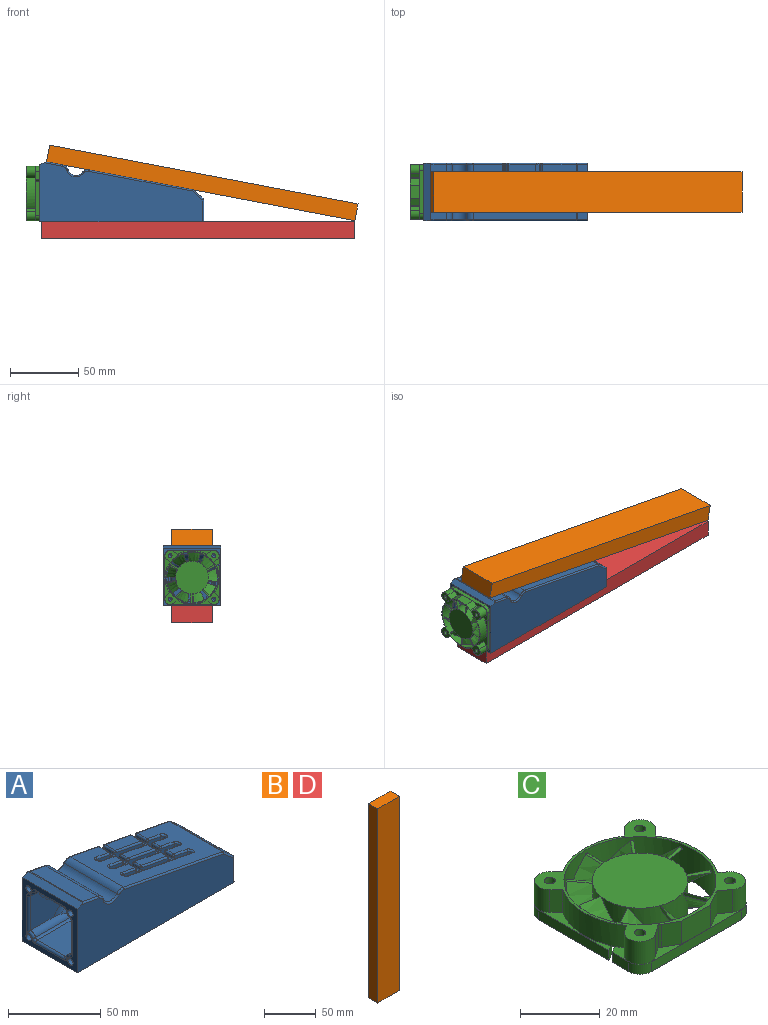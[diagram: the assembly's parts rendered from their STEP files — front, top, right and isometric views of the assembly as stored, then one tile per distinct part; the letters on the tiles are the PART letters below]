
ASSEMBLY  parts=4 mates=1
PART A: 266 faces, bbox 123.9x42.9x45.2 mm
  f0: plane 119.42x43.31mm, normal (0,-1,0), area 3799.1mm2, adj f2,f18,f19,f95,f96,f102,f110,f111
  f1: plane 119.42x43.31mm, normal (0,1,0), area 3711mm2, adj f2,f18,f19,f24,f26,f28,f75,f82
  f2: plane 42x42mm, normal (-1,0,0), area 549mm2, adj f0,f1,f18,f19,f43,f45,f47,f49
  f3: plane 28.92x13.78mm, normal (-1,0,0), area 281.8mm2, adj f10,f29,f78,f80,f81,f222,f223,f259
  f4: plane 75.7x40mm, normal (0.19,0,0.98), area 1748.4mm2, adj f103,f111,f118,f125,f131,f138,f139,f144
  f5: plane 19.65x5mm, normal (0.19,0,0.98), area 100mm2, adj f167,f168,f184,f185
  f6: plane 19.65x5mm, normal (0.19,0,0.98), area 100mm2, adj f107,f115,f121,f122
  f7: plane 19.65x7.5mm, normal (0.19,0,0.98), area 150mm2, adj f82,f84,f86,f87
  f8: plane 49.86x13.29mm, normal (0,1,0), area 175.6mm2, adj f29,f50,f52,f69,f107,f120,f127,f132
  f9: plane 49.86x13.29mm, normal (0,1,0), area 173.4mm2, adj f29,f53,f55,f155,f159,f164,f168,f174
  f10: plane 113.99x26.84mm, normal (0,0,1), area 2764.6mm2, adj f3,f15,f32,f33,f34,f35,f223,f246
  f11: cone r=2.58mm half-angle=59deg, axis (0,1,0), area 59.4mm2, adj f12,f40,f246,f249
  f12: torus R=11.59mm, axis (0,-1,0), area 95.8mm2, adj f11,f15,f40,f246
  f13: plane 21.06x5.74mm, normal (-0.19,0,-0.98), area 122.8mm2, adj f14,f36,f229,f232
  f14: plane 21.11x3.44mm, normal (0.37,0,-0.93), area 78mm2, adj f13,f229,f230,f232,f236,f237
  f15: plane 111.92x26.52mm, normal (0,-1,0), area 1378.2mm2, adj f10,f12,f16,f34,f35,f40,f223,f225
  f16: torus R=21mm, axis (0,-1,0), area 471.5mm2, adj f15,f30,f36,f227,f231,f234
  f17: plane 40x11.7mm, normal (0.19,0,0.98), area 476.4mm2, adj f90,f91,f96,f264
  f18: plane 42.19x4.92mm, normal (-0.37,0,0.93), area 213.5mm2, adj f0,f1,f2,f90,f91,f96
  f19: plane 119.42x42mm, normal (0,0,-1), area 5015.7mm2, adj f0,f1,f2,f100
  f20: plane 40x15.04mm, normal (1,0,0), area 601.6mm2, adj f95,f100,f108,f109
  f21: plane 40x7.68mm, normal (0.65,0,0.76), area 219.4mm2, adj f109,f110,f124,f125,f218,f219,f220,f221
  f22: cylinder r=6mm len=40mm, axis (0,1,0), area 527.5mm2, adj f97,f102,f261,f264
  f23: cone r=0mm half-angle=59deg, axis (0,1,0), area 24.8mm2, adj f24
  f24: cylinder r=2.6mm len=5.2mm, axis (0,1,0), area 49mm2, adj f1,f23
  f25: cone r=0mm half-angle=59deg, axis (0,1,0), area 24.8mm2, adj f26
  f26: cylinder r=2.6mm len=5.2mm, axis (0,1,0), area 49mm2, adj f1,f25
  f27: cone r=0mm half-angle=59deg, axis (0,1,0), area 24.8mm2, adj f28
  f28: cylinder r=2.6mm len=5.2mm, axis (0,1,0), area 49mm2, adj f1,f27
  f29: plane 79.71x28.72mm, normal (-0.19,0,-0.98), area 1654.8mm2, adj f3,f8,f9,f50,f51,f52,f53,f54
  f30: cylinder r=11mm len=17.03mm, axis (0,1,0), area 234.6mm2, adj f16,f36,f37,f228
  f31: plane 111.92x21.42mm, normal (0,1,0), area 1445.6mm2, adj f37,f222,f224,f243,f250,f255
  f32: cone r=2.58mm half-angle=59deg, axis (0,1,0), area 90.4mm2, adj f10,f35
  f33: cone r=2.58mm half-angle=59deg, axis (0,1,0), area 90.4mm2, adj f10,f34
  f34: torus R=11.59mm, axis (0,-1,0), area 115.8mm2, adj f10,f15,f33
  f35: torus R=11.59mm, axis (0,-1,0), area 115.8mm2, adj f10,f15,f32
  f36: cylinder r=10mm len=21.64mm, axis (0,1,0), area 148.6mm2, adj f13,f16,f30,f37,f231,f235
  f37: torus R=21mm, axis (0,-1,0), area 471.5mm2, adj f30,f31,f36,f226,f235,f240
  f38: cylinder r=4mm len=12.05mm, axis (-1,0,0), area 55.1mm2, adj f229,f230,f231,f234,f238,f239
  f39: cylinder r=4mm len=12.05mm, axis (-1,0,0), area 55.1mm2, adj f232,f235,f236,f240,f243,f244
  f40: cylinder r=4mm len=26.78mm, axis (-1,0,0), area 120.5mm2, adj f11,f12,f15,f248,f249
  f41: cylinder r=4mm len=112.42mm, axis (-1,0,0), area 441.4mm2, adj f253,f255,f257,f258,f259
  f42: cone r=0mm half-angle=59deg, axis (-1,0,0), area 14.7mm2, adj f43
  f43: cylinder r=2mm len=12mm, axis (-1,0,0), area 150.8mm2, adj f2,f42
  f44: cone r=0mm half-angle=59deg, axis (-1,0,0), area 14.7mm2, adj f45
  f45: cylinder r=2mm len=12mm, axis (-1,0,0), area 150.8mm2, adj f2,f44
  f46: cone r=0mm half-angle=59deg, axis (-1,0,0), area 14.7mm2, adj f47
  f47: cylinder r=2mm len=12mm, axis (-1,0,0), area 150.8mm2, adj f2,f46
  f48: cone r=0mm half-angle=59deg, axis (-1,0,0), area 14.7mm2, adj f49
  f49: cylinder r=2mm len=12mm, axis (-1,0,0), area 150.8mm2, adj f2,f48
  f50: cylinder r=1.5mm len=4.21mm, axis (0.19,0,0.98), area 18.8mm2, adj f8,f29,f51,f162
  f51: plane 49.86x13.29mm, normal (0,-1,0), area 175.6mm2, adj f29,f50,f52,f75,f87,f94,f99,f106
  f52: cylinder r=1.5mm len=4.21mm, axis (0.19,0,0.98), area 18.8mm2, adj f8,f29,f51,f139
  f53: cylinder r=1.5mm len=4.21mm, axis (0.19,0,0.98), area 18.8mm2, adj f9,f29,f54,f203
  f54: plane 49.86x13.29mm, normal (0,-1,0), area 175.6mm2, adj f29,f53,f55,f69,f122,f134,f141,f147
  f55: cylinder r=1.5mm len=4.21mm, axis (0.19,0,0.98), area 18.8mm2, adj f9,f29,f54,f173
  f56: cylinder r=1.5mm len=4.21mm, axis (0.19,0,0.98), area 18.8mm2, adj f29,f57,f59,f215
  f57: plane 49.86x13.29mm, normal (0,-1,0), area 173.4mm2, adj f29,f56,f58,f166,f175,f183,f184,f190
  f58: cylinder r=1.5mm len=4.21mm, axis (0.19,0,0.98), area 18.8mm2, adj f29,f57,f59,f209
  f59: plane 49.86x13.29mm, normal (0,1,0), area 200mm2, adj f29,f56,f58,f212
  f60: plane 5x0.98mm, normal (-0.98,0,0.19), area 5mm2, adj f155,f165,f166,f167
  f61: plane 5x0.98mm, normal (0.98,0,-0.19), area 5mm2, adj f181,f182,f194,f195
  f62: plane 5x0.98mm, normal (0.19,0,0.98), area 5mm2, adj f164,f165,f182,f183
  f63: plane 5x0.98mm, normal (0.98,0,-0.19), area 5mm2, adj f185,f186,f196,f197
  f64: plane 5x0.98mm, normal (-0.98,0,0.19), area 5mm2, adj f206,f207,f213,f214
  f65: plane 5x0.98mm, normal (0.19,0,0.98), area 5mm2, adj f197,f198,f205,f206
  f66: plane 5x0.98mm, normal (-0.98,0,0.19), area 5mm2, adj f120,f121,f133,f134
  f67: plane 5x0.98mm, normal (0.98,0,-0.19), area 5mm2, adj f145,f146,f153,f154
  f68: plane 5x0.98mm, normal (0.19,0,0.98), area 5mm2, adj f132,f133,f146,f147
  f69: plane 7x2.95mm, normal (0.98,0,-0.19), area 14.4mm2, adj f8,f54,f71,f115,f156,f169
  f70: plane 5x0.98mm, normal (-0.98,0,0.19), area 5mm2, adj f170,f171,f187,f188
  f71: plane 5x1.96mm, normal (0.19,0,0.98), area 10mm2, adj f69,f156,f169,f170
  f72: plane 7.5x0.98mm, normal (-0.98,0,0.19), area 7.5mm2, adj f85,f86,f93,f94
  f73: plane 7.5x0.98mm, normal (0.98,0,-0.19), area 7.5mm2, adj f104,f105,f118,f119
  f74: plane 7.5x0.98mm, normal (0.19,0,0.98), area 7.5mm2, adj f92,f93,f105,f106
  f75: plane 9.5x2.95mm, normal (0.98,0,-0.19), area 19.4mm2, adj f1,f51,f77,f84,f123,f135
  f76: plane 7.5x0.98mm, normal (-0.98,0,0.19), area 7.5mm2, adj f136,f137,f148,f149
  f77: plane 7.5x1.96mm, normal (0.19,0,0.98), area 15mm2, adj f75,f123,f135,f136
  f78: cylinder r=2.5mm len=5.92mm, axis (0.65,0,0.76), area 17.2mm2, adj f3,f29,f79,f80,f221
  f79: plane 21x2.34mm, normal (0.76,0,-0.65), area 64.8mm2, adj f29,f78,f81,f220
  f80: plane 21x2.48mm, normal (-0.76,0,0.65), area 68.7mm2, adj f3,f78,f81,f219
  f81: cylinder r=2.5mm len=5.92mm, axis (0.65,0,0.76), area 17.2mm2, adj f3,f29,f79,f80,f218
  f82: cylinder r=1mm len=20.82mm, axis (-0.98,0,0.19), area 32.2mm2, adj f1,f7,f83,f84
  f83: sphere r=1mm, area 1.6mm2, adj f82,f85,f86
  f84: cylinder r=1mm len=9.5mm, axis (0,-1,0), area 13.4mm2, adj f7,f75,f82,f87
  f85: cylinder r=1mm len=1.17mm, axis (0.19,0,0.98), area 1.6mm2, adj f1,f72,f83,f88
  f86: cylinder r=1mm len=7.5mm, axis (0,1,0), area 11.8mm2, adj f7,f72,f83,f89
  f87: cylinder r=1mm len=20.82mm, axis (-0.98,0,0.19), area 32.2mm2, adj f7,f51,f84,f89
  f88: torus R=2mm, axis (0,-1,0), area 3.4mm2, adj f1,f85,f92,f93
  f89: sphere r=1mm, area 1.6mm2, adj f86,f87,f94
  f90: cylinder r=1mm len=41.08mm, axis (0,1,0), area 23.1mm2, adj f17,f18,f91,f96
  f91: cylinder r=1mm len=13.71mm, axis (-0.98,0,0.19), area 20.1mm2, adj f1,f17,f18,f90,f265
  f92: cylinder r=1mm len=1.17mm, axis (0.98,0,-0.19), area 1.6mm2, adj f1,f74,f88,f98
  f93: cylinder r=1mm len=7.5mm, axis (0,1,0), area 11.8mm2, adj f72,f74,f88,f99
  f94: cylinder r=1mm len=1.17mm, axis (0.19,0,0.98), area 1.6mm2, adj f51,f72,f89,f99
  f95: cylinder r=1mm len=16.04mm, axis (0,0,-1), area 24.4mm2, adj f0,f20,f100,f101
  f96: cylinder r=1mm len=13.71mm, axis (0.98,0,-0.19), area 20.1mm2, adj f0,f17,f18,f90,f263
  f97: torus R=7mm, axis (0,-1,0), area 22mm2, adj f1,f22,f262,f265
  f98: torus R=2mm, axis (0,-1,0), area 3.4mm2, adj f1,f92,f104,f105
  f99: torus R=2mm, axis (0,1,0), area 3.4mm2, adj f51,f93,f94,f106
  f100: cylinder r=1mm len=42mm, axis (0,-1,0), area 64.4mm2, adj f19,f20,f95,f108
  f101: sphere r=1mm, area 0.9mm2, adj f95,f109,f110
  f102: torus R=7mm, axis (0,-1,0), area 22mm2, adj f0,f22,f260,f263
  f103: cylinder r=1mm len=21.57mm, axis (-0.98,0,0.19), area 34.2mm2, adj f1,f4,f112,f262
  f104: cylinder r=1mm len=1.17mm, axis (-0.19,0,-0.98), area 1.6mm2, adj f1,f73,f98,f112
  f105: cylinder r=1mm len=7.5mm, axis (0,-1,0), area 11.8mm2, adj f73,f74,f98,f113
  f106: cylinder r=1mm len=1.17mm, axis (0.98,0,-0.19), area 1.6mm2, adj f51,f74,f99,f113
  f107: cylinder r=1mm len=20.82mm, axis (0.98,0,-0.19), area 32.2mm2, adj f6,f8,f114,f115
  f108: cylinder r=1mm len=16.04mm, axis (0,0,1), area 24.4mm2, adj f1,f20,f100,f116
  f109: cylinder r=1mm len=40mm, axis (0,-1,0), area 34.4mm2, adj f20,f21,f101,f116
  f110: cylinder r=1mm len=8.33mm, axis (0.76,0,-0.65), area 15.9mm2, adj f0,f21,f101,f117
  f111: cylinder r=1mm len=75.88mm, axis (0.98,0,-0.19), area 121mm2, adj f0,f4,f117,f260
  f112: sphere r=1mm, area 1.1mm2, adj f103,f104,f118
  f113: torus R=2mm, axis (0,1,0), area 3.4mm2, adj f51,f105,f106,f119
  f114: sphere r=1mm, area 1.6mm2, adj f107,f120,f121
  f115: cylinder r=1mm len=7mm, axis (0,-1,0), area 9.4mm2, adj f6,f69,f107,f122
  f116: sphere r=1mm, area 0.9mm2, adj f108,f109,f124
  f117: sphere r=1mm, area 0.5mm2, adj f110,f111,f125
  f118: cylinder r=1mm len=7.5mm, axis (0,-1,0), area 11.8mm2, adj f4,f73,f112,f126
  f119: cylinder r=1mm len=1.17mm, axis (-0.19,0,-0.98), area 1.6mm2, adj f51,f73,f113,f126
  f120: cylinder r=1mm len=1.17mm, axis (-0.19,0,-0.98), area 1.6mm2, adj f8,f66,f114,f127
  f121: cylinder r=1mm len=5mm, axis (0,1,0), area 7.9mm2, adj f6,f66,f114,f128
  f122: cylinder r=1mm len=20.82mm, axis (-0.98,0,0.19), area 32.2mm2, adj f6,f54,f115,f128
  f123: cylinder r=1mm len=2.15mm, axis (0.98,0,-0.19), area 3.1mm2, adj f1,f75,f77,f129
  f124: cylinder r=1mm len=8.33mm, axis (-0.76,0,0.65), area 15.9mm2, adj f1,f21,f116,f130
  f125: cylinder r=1mm len=40mm, axis (0,1,0), area 20.9mm2, adj f4,f21,f117,f130
  f126: sphere r=1mm, area 1.1mm2, adj f118,f119,f131
  f127: torus R=2mm, axis (0,1,0), area 3.4mm2, adj f8,f120,f132,f133
  f128: sphere r=1mm, area 1.6mm2, adj f121,f122,f134
  f129: torus R=2mm, axis (0,-1,0), area 3.4mm2, adj f1,f123,f136,f137
  f130: sphere r=1mm, area 0.8mm2, adj f124,f125,f138
  f131: cylinder r=1mm len=10.01mm, axis (-0.98,0,0.19), area 15.7mm2, adj f4,f51,f126,f139
  f132: cylinder r=1mm len=1.17mm, axis (-0.98,0,0.19), area 1.6mm2, adj f8,f68,f127,f140
  f133: cylinder r=1mm len=5mm, axis (0,1,0), area 7.9mm2, adj f66,f68,f127,f141
  f134: cylinder r=1mm len=1.17mm, axis (0.19,0,0.98), area 1.6mm2, adj f54,f66,f128,f141
  f135: cylinder r=1mm len=2.15mm, axis (-0.98,0,0.19), area 3.1mm2, adj f51,f75,f77,f142
  f136: cylinder r=1mm len=7.5mm, axis (0,1,0), area 11.8mm2, adj f76,f77,f129,f142
  f137: cylinder r=1mm len=1.17mm, axis (0.19,0,0.98), area 1.6mm2, adj f1,f76,f129,f143
  f138: cylinder r=1mm len=25.03mm, axis (-0.98,0,0.19), area 39.7mm2, adj f1,f4,f130,f143
  f139: torus R=2.5mm, axis (-0.19,0,-0.98), area 9.2mm2, adj f4,f52,f131,f144
  f140: torus R=2mm, axis (0,1,0), area 3.4mm2, adj f8,f132,f145,f146
  f141: torus R=2mm, axis (0,1,0), area 3.4mm2, adj f54,f133,f134,f147
  f142: torus R=2mm, axis (0,1,0), area 3.4mm2, adj f51,f135,f136,f148
  f143: sphere r=1mm, area 1.6mm2, adj f137,f138,f149
  f144: cylinder r=1mm len=10.01mm, axis (0.98,0,-0.19), area 15.7mm2, adj f4,f8,f139,f150
  f145: cylinder r=1mm len=1.17mm, axis (0.19,0,0.98), area 1.6mm2, adj f8,f67,f140,f150
  f146: cylinder r=1mm len=5mm, axis (0,-1,0), area 7.9mm2, adj f67,f68,f140,f151
  f147: cylinder r=1mm len=1.17mm, axis (0.98,0,-0.19), area 1.6mm2, adj f54,f68,f141,f151
  f148: cylinder r=1mm len=1.17mm, axis (0.19,0,0.98), area 1.6mm2, adj f51,f76,f142,f152
  f149: cylinder r=1mm len=7.5mm, axis (0,1,0), area 11.8mm2, adj f4,f76,f143,f152
  f150: sphere r=1mm, area 1.1mm2, adj f144,f145,f153
  f151: torus R=2mm, axis (0,1,0), area 3.4mm2, adj f54,f146,f147,f154
  f152: sphere r=1mm, area 1.6mm2, adj f148,f149,f157
  f153: cylinder r=1mm len=5mm, axis (0,-1,0), area 7.9mm2, adj f4,f67,f150,f158
  f154: cylinder r=1mm len=1.17mm, axis (-0.19,0,-0.98), area 1.6mm2, adj f54,f67,f151,f158
  f155: cylinder r=1mm len=1.17mm, axis (-0.19,0,-0.98), area 1.6mm2, adj f9,f60,f159,f160
  f156: cylinder r=1mm len=2.15mm, axis (0.98,0,-0.19), area 3.1mm2, adj f8,f69,f71,f161
  f157: cylinder r=1mm len=10.01mm, axis (-0.98,0,0.19), area 15.7mm2, adj f4,f51,f152,f162
  f158: sphere r=1mm, area 1.1mm2, adj f153,f154,f163
  f159: torus R=2mm, axis (0,1,0), area 3.4mm2, adj f9,f155,f164,f165
  f160: sphere r=1mm, area 1.6mm2, adj f155,f167,f168
  f161: torus R=2mm, axis (0,1,0), area 3.4mm2, adj f8,f156,f170,f171
  f162: torus R=2.5mm, axis (-0.19,0,-0.98), area 9.2mm2, adj f4,f50,f157,f172
  f163: cylinder r=1mm len=10.01mm, axis (-0.98,0,0.19), area 15.7mm2, adj f4,f54,f158,f173
  f164: cylinder r=1mm len=1.17mm, axis (-0.98,0,0.19), area 1.6mm2, adj f9,f62,f159,f174
  f165: cylinder r=1mm len=5mm, axis (0,1,0), area 7.9mm2, adj f60,f62,f159,f175
  f166: cylinder r=1mm len=1.17mm, axis (0.19,0,0.98), area 1.6mm2, adj f57,f60,f175,f176
  f167: cylinder r=1mm len=5mm, axis (0,1,0), area 7.9mm2, adj f5,f60,f160,f176
  f168: cylinder r=1mm len=19.83mm, axis (0.98,0,-0.19), area 31.4mm2, adj f5,f9,f160,f177
  f169: cylinder r=1mm len=2.15mm, axis (-0.98,0,0.19), area 3.1mm2, adj f54,f69,f71,f178
  f170: cylinder r=1mm len=5mm, axis (0,1,0), area 7.9mm2, adj f70,f71,f161,f178
  f171: cylinder r=1mm len=1.17mm, axis (-0.19,0,-0.98), area 1.6mm2, adj f8,f70,f161,f179
  f172: cylinder r=1mm len=10.01mm, axis (0.98,0,-0.19), area 15.7mm2, adj f4,f8,f162,f179
  f173: torus R=2.5mm, axis (-0.19,0,-0.98), area 9.2mm2, adj f4,f55,f163,f180
  f174: torus R=2mm, axis (0,1,0), area 3.4mm2, adj f9,f164,f181,f182
  f175: torus R=2mm, axis (0,1,0), area 3.4mm2, adj f57,f165,f166,f183
  f176: sphere r=1mm, area 1.6mm2, adj f166,f167,f184
  f177: sphere r=1mm, area 1.1mm2, adj f168,f185,f186
  f178: torus R=2mm, axis (0,1,0), area 3.4mm2, adj f54,f169,f170,f187
  f179: sphere r=1mm, area 1.6mm2, adj f171,f172,f188
  f180: cylinder r=1mm len=10.01mm, axis (0.98,0,-0.19), area 15.7mm2, adj f4,f9,f173,f189
  f181: cylinder r=1mm len=1.17mm, axis (0.19,0,0.98), area 1.6mm2, adj f9,f61,f174,f189
  f182: cylinder r=1mm len=5mm, axis (0,-1,0), area 7.9mm2, adj f61,f62,f174,f190
  f183: cylinder r=1mm len=1.17mm, axis (0.98,0,-0.19), area 1.6mm2, adj f57,f62,f175,f190
  f184: cylinder r=1mm len=19.83mm, axis (-0.98,0,0.19), area 31.4mm2, adj f5,f57,f176,f191
  f185: cylinder r=1mm len=5mm, axis (0,-1,0), area 7.9mm2, adj f5,f63,f177,f191
  f186: cylinder r=1mm len=1.17mm, axis (0.19,0,0.98), area 1.6mm2, adj f9,f63,f177,f192
  f187: cylinder r=1mm len=1.17mm, axis (0.19,0,0.98), area 1.6mm2, adj f54,f70,f178,f193
  f188: cylinder r=1mm len=5mm, axis (0,1,0), area 7.9mm2, adj f4,f70,f179,f193
  f189: sphere r=1mm, area 1.1mm2, adj f180,f181,f194
  f190: torus R=2mm, axis (0,1,0), area 3.4mm2, adj f57,f182,f183,f195
  f191: sphere r=1mm, area 1.6mm2, adj f184,f185,f196
  f192: torus R=2mm, axis (0,1,0), area 3.4mm2, adj f9,f186,f197,f198
  f193: sphere r=1mm, area 1.6mm2, adj f187,f188,f199
  f194: cylinder r=1mm len=5mm, axis (0,-1,0), area 7.9mm2, adj f4,f61,f189,f200
  f195: cylinder r=1mm len=1.17mm, axis (-0.19,0,-0.98), area 1.6mm2, adj f57,f61,f190,f200
  f196: cylinder r=1mm len=1.17mm, axis (-0.19,0,-0.98), area 1.6mm2, adj f57,f63,f191,f201
  f197: cylinder r=1mm len=5mm, axis (0,-1,0), area 7.9mm2, adj f63,f65,f192,f201
  f198: cylinder r=1mm len=1.17mm, axis (0.98,0,-0.19), area 1.6mm2, adj f9,f65,f192,f202
  f199: cylinder r=1mm len=10.01mm, axis (-0.98,0,0.19), area 15.7mm2, adj f4,f54,f193,f203
  f200: sphere r=1mm, area 1.1mm2, adj f194,f195,f204
  f201: torus R=2mm, axis (0,1,0), area 3.4mm2, adj f57,f196,f197,f205
  f202: torus R=2mm, axis (0,1,0), area 3.4mm2, adj f9,f198,f206,f207
  f203: torus R=2.5mm, axis (-0.19,0,-0.98), area 9.2mm2, adj f4,f53,f199,f208
  f204: cylinder r=1mm len=10.01mm, axis (-0.98,0,0.19), area 15.7mm2, adj f4,f57,f200,f209
  f205: cylinder r=1mm len=1.17mm, axis (-0.98,0,0.19), area 1.6mm2, adj f57,f65,f201,f210
  f206: cylinder r=1mm len=5mm, axis (0,1,0), area 7.9mm2, adj f64,f65,f202,f210
  f207: cylinder r=1mm len=1.17mm, axis (-0.19,0,-0.98), area 1.6mm2, adj f9,f64,f202,f211
  f208: cylinder r=1mm len=10.01mm, axis (0.98,0,-0.19), area 15.7mm2, adj f4,f9,f203,f211
  f209: torus R=2.5mm, axis (-0.19,0,-0.98), area 9.2mm2, adj f4,f58,f204,f212
  f210: torus R=2mm, axis (0,1,0), area 3.4mm2, adj f57,f205,f206,f213
  f211: sphere r=1mm, area 1.6mm2, adj f207,f208,f214
  f212: cylinder r=1mm len=49.3mm, axis (0.98,0,-0.19), area 78.5mm2, adj f4,f59,f209,f215
  f213: cylinder r=1mm len=1.17mm, axis (0.19,0,0.98), area 1.6mm2, adj f57,f64,f210,f216
  f214: cylinder r=1mm len=5mm, axis (0,1,0), area 7.9mm2, adj f4,f64,f211,f216
  f215: torus R=2.5mm, axis (-0.19,0,-0.98), area 9.2mm2, adj f4,f56,f212,f217
  f216: sphere r=1mm, area 1.6mm2, adj f213,f214,f217
  f217: cylinder r=1mm len=10.01mm, axis (-0.98,0,0.19), area 15.7mm2, adj f4,f57,f215,f216
  f218: torus R=3.5mm, axis (-0.65,0,-0.76), area 14.1mm2, adj f21,f81,f219,f220
  f219: cylinder r=1mm len=21mm, axis (0,1,0), area 33mm2, adj f21,f80,f218,f221
  f220: cylinder r=1mm len=21mm, axis (0,-1,0), area 33mm2, adj f21,f79,f218,f221
  f221: torus R=3.5mm, axis (-0.65,0,-0.76), area 14.1mm2, adj f21,f78,f219,f220
  f222: cylinder r=2mm len=7.93mm, axis (0,0,1), area 22.1mm2, adj f3,f31,f224,f257
  f223: cylinder r=2mm len=12.86mm, axis (0,0,-1), area 37.8mm2, adj f3,f10,f15,f225
  f224: cylinder r=2mm len=70.67mm, axis (-0.98,0,0.19), area 222.2mm2, adj f29,f31,f222,f226
  f225: cylinder r=2mm len=70.67mm, axis (0.98,0,-0.19), area 222.2mm2, adj f15,f29,f223,f227
  f226: bspline ~12.88x12.05mm, area 37.4mm2, adj f29,f37,f224,f228
  f227: bspline ~12.88x12.05mm, area 37.4mm2, adj f16,f29,f225,f228
  f228: cylinder r=2mm len=12mm, axis (0,1,0), area 24.1mm2, adj f29,f30,f226,f227
  f229: bspline ~6.02x2.42mm, area 13.3mm2, adj f13,f14,f38,f230,f231
  f230: bspline ~7.09x3.55mm, area 9.4mm2, adj f14,f38,f229,f233
  f231: bspline ~5.61x2.72mm, area 7mm2, adj f16,f36,f38,f229,f234
  f232: bspline ~6.02x2.42mm, area 13.3mm2, adj f13,f14,f39,f235,f236
  f233: bspline ~3.41x3.02mm, area 7.8mm2, adj f2,f230,f237,f238
  f234: bspline ~9.45x5.23mm, area 14.6mm2, adj f16,f38,f231,f239
  f235: bspline ~5.61x2.72mm, area 7mm2, adj f36,f37,f39,f232,f240
  f236: bspline ~7.09x3.55mm, area 9.4mm2, adj f14,f39,f232,f241
  f237: cylinder r=1.5mm len=21.11mm, axis (0,-1,0), area 61.8mm2, adj f2,f14,f233,f241
  f238: torus R=2.5mm, axis (1,0,0), area 8.7mm2, adj f2,f38,f233,f242
  f239: cylinder r=1.5mm len=5.85mm, axis (-1,0,0), area 11.4mm2, adj f15,f38,f234,f242
  f240: bspline ~8.39x5.21mm, area 14.6mm2, adj f37,f39,f235,f243
  f241: bspline ~3.71x3.23mm, area 7.8mm2, adj f2,f236,f237,f244
  f242: torus R=3mm, axis (1,0,0), area 6.2mm2, adj f2,f238,f239,f245
  f243: cylinder r=1.5mm len=5.85mm, axis (-1,0,0), area 11.4mm2, adj f31,f39,f240,f247
  f244: torus R=2.5mm, axis (1,0,0), area 8.7mm2, adj f2,f39,f241,f247
  f245: cylinder r=1.5mm len=24.71mm, axis (0,0,1), area 55.9mm2, adj f2,f15,f242,f248
  f246: bspline ~16.52x8.29mm, area 24mm2, adj f10,f11,f12,f15,f249
  f247: torus R=3mm, axis (1,0,0), area 6.2mm2, adj f2,f243,f244,f250
  f248: torus R=2.5mm, axis (1,0,0), area 12.7mm2, adj f2,f40,f245,f251
  f249: cylinder r=1.5mm len=26.78mm, axis (-1,0,0), area 50.3mm2, adj f10,f11,f40,f246,f251
  f250: cylinder r=1.5mm len=21.42mm, axis (0,0,-1), area 50.5mm2, adj f2,f31,f247,f252
  f251: torus R=3mm, axis (1,0,0), area 6.1mm2, adj f2,f248,f249,f254
  f252: torus R=3mm, axis (1,0,0), area 6.2mm2, adj f2,f250,f253,f255
  f253: torus R=2.5mm, axis (1,0,0), area 8mm2, adj f2,f41,f252,f256
  f254: cylinder r=1.5mm len=21.53mm, axis (0,-1,0), area 50.7mm2, adj f2,f10,f251,f256
  f255: cylinder r=1.5mm len=111.92mm, axis (-1,0,0), area 217.3mm2, adj f31,f41,f252,f257
  f256: torus R=3mm, axis (1,0,0), area 6.1mm2, adj f2,f253,f254,f258
  f257: bspline ~2.52x2.48mm, area 4.4mm2, adj f41,f222,f255,f259
  f258: cylinder r=1.5mm len=113.9mm, axis (-1,0,0), area 213.5mm2, adj f10,f41,f256,f259
  f259: torus R=5.5mm, axis (1,0,0), area 11.6mm2, adj f3,f10,f41,f257,f258
  f260: torus R=4mm, axis (0,-1,0), area 8mm2, adj f0,f102,f111,f261
  f261: cylinder r=5mm len=40mm, axis (0,1,0), area 219.8mm2, adj f4,f22,f260,f262
  f262: torus R=4mm, axis (0,-1,0), area 8mm2, adj f1,f97,f103,f261
  f263: torus R=4mm, axis (0,-1,0), area 8mm2, adj f0,f96,f102,f264
  f264: cylinder r=5mm len=40mm, axis (0,1,0), area 219.8mm2, adj f17,f22,f263,f265
  f265: torus R=4mm, axis (0,-1,0), area 8mm2, adj f1,f91,f97,f264
PART B: 6 faces, bbox 30x12.5x230 mm
  f0: plane 230x12.5mm, normal (1,0,0), area 2875mm2, adj f1,f3,f4,f5
  f1: plane 230x30mm, normal (0,1,0), area 6900mm2, adj f0,f2,f4,f5
  f2: plane 230x12.5mm, normal (-1,0,0), area 2875mm2, adj f1,f3,f4,f5
  f3: plane 230x30mm, normal (0,-1,0), area 6900mm2, adj f0,f2,f4,f5
  f4: plane 30x12.5mm, normal (0,0,1), area 375mm2, adj f0,f1,f2,f3
  f5: plane 30x12.5mm, normal (0,0,-1), area 375mm2, adj f0,f1,f2,f3
PART C: 104 faces, bbox 40x40x10 mm
  f0: plane 4.98x4.18mm, normal (0.64,0.77,0), area 6.5mm2, adj f2,f3,f4,f24
  f1: plane 6.11x2.22mm, normal (-0.94,-0.34,0), area 6.5mm2, adj f2,f3,f4,f5
  f2: bspline ~9x7.84mm, area 9.7mm2, adj f0,f1,f3,f4
  f3: bspline ~10.07x9.67mm, area 73.6mm2, adj f0,f1,f2,f24
  f4: bspline ~10.07x9.67mm, area 73.6mm2, adj f0,f1,f2,f5
  f5: cylinder r=12mm len=13.3mm, axis (0,0,-1), area 69.1mm2, adj f1,f4,f6,f9,f74,f75
  f6: plane 6.4x1.13mm, normal (0.98,0.17,0), area 6.5mm2, adj f5,f8,f9,f10
  f7: plane 6.11x2.22mm, normal (-0.94,0.34,0), area 6.5mm2, adj f8,f9,f10,f11
  f8: bspline ~9.54x9mm, area 9.7mm2, adj f6,f7,f9,f10
  f9: bspline ~9.54x8mm, area 73.6mm2, adj f5,f6,f7,f8
  f10: bspline ~9.54x8mm, area 73.6mm2, adj f6,f7,f8,f11
  f11: cylinder r=12mm len=12.48mm, axis (0,0,-1), area 69.1mm2, adj f7,f10,f12,f15,f74,f75
  f12: plane 5.63x3.25mm, normal (0.87,-0.5,0), area 6.5mm2, adj f11,f14,f15,f16
  f13: plane 5.63x3.25mm, normal (-0.5,0.87,0), area 6.5mm2, adj f14,f15,f16,f17
  f14: bspline ~9x6.77mm, area 9.7mm2, adj f12,f13,f15,f16
  f15: bspline ~10.02x10.02mm, area 73.6mm2, adj f11,f12,f13,f14
  f16: bspline ~10.02x10.02mm, area 73.6mm2, adj f12,f13,f14,f17
  f17: cylinder r=12mm len=12.48mm, axis (0,0,-1), area 69.1mm2, adj f13,f16,f18,f21,f25,f74,f75,f76
  f18: plane 6.11x2.22mm, normal (0.34,-0.94,0), area 6.5mm2, adj f17,f20,f21,f22
  f19: plane 6.4x1.13mm, normal (0.17,0.98,0), area 6.5mm2, adj f20,f21,f22,f24
  f20: bspline ~9.54x9mm, area 9.7mm2, adj f18,f19,f21,f22
  f21: bspline ~9.54x8mm, area 73.6mm2, adj f17,f18,f19,f20
  f22: bspline ~9.54x8mm, area 73.6mm2, adj f18,f19,f20,f24
  f23: plane 5.9x3mm, normal (-1,0,0), area 17.7mm2, adj f39,f40,f52,f72
  f24: cylinder r=12mm len=24mm, axis (0,0,-1), area 416.7mm2, adj f0,f3,f19,f22,f26,f27,f73,f74
  f25: plane 7.42x5.73mm, normal (0,0,1), area 17.8mm2, adj f17,f28,f71,f72
  f26: plane 7.42x5.73mm, normal (0,0,1), area 17.8mm2, adj f24,f28,f69,f70
  f27: plane 7.17x2.5mm, normal (0,0,1), area 17.8mm2, adj f24,f28,f66,f67
  f28: cylinder r=19.1mm len=38.2mm, axis (0,0,1), area 1189.6mm2, adj f25,f26,f27,f33,f40,f66,f67,f69
  f29: cylinder r=11mm len=17.68mm, axis (0,0,-1), area 20.5mm2, adj f40,f70,f71,f74
  f30: cylinder r=11mm len=15.31mm, axis (0,0,-1), area 20.5mm2, adj f40,f67,f69,f73
  f31: plane 32x3mm, normal (0,1,0), area 96mm2, adj f36,f38,f40,f52
  f32: plane 32x3mm, normal (0,-1,0), area 96mm2, adj f35,f39,f40,f52
  f33: plane 39.8x39.8mm, normal (0,0,1), area 255.1mm2, adj f28,f41,f42,f43,f44,f45,f46,f47
  f34: plane 32x3mm, normal (1,0,0), area 96mm2, adj f35,f36,f40,f52
  f35: cylinder r=4mm len=4mm, axis (0,0,-1), area 18.8mm2, adj f32,f34,f40,f52
  f36: cylinder r=4mm len=4mm, axis (0,0,-1), area 18.8mm2, adj f31,f34,f40,f52
  f37: plane 24.95x3mm, normal (-1,0,0), area 74.8mm2, adj f38,f40,f52,f103
  f38: cylinder r=4mm len=4mm, axis (0,0,-1), area 18.8mm2, adj f31,f37,f40,f52
  f39: cylinder r=4mm len=4mm, axis (0,0,-1), area 18.8mm2, adj f23,f32,f40,f52
  f40: plane 40x40mm, normal (0,0,-1), area 853.4mm2, adj f23,f28,f29,f30,f31,f32,f34,f35
  f41: cylinder r=3.9mm len=7.09mm, axis (0,0,1), area 85.8mm2, adj f33,f42,f51,f52
  f42: plane 7x3.35mm, normal (0.57,-0.82,0), area 28.6mm2, adj f33,f41,f43,f52
  f43: cylinder r=19.8mm len=7mm, axis (0,0,1), area 5.8mm2, adj f33,f42,f44,f52
  f44: plane 7x4.69mm, normal (-0.49,-0.87,0), area 37.7mm2, adj f33,f43,f45,f52
  f45: plane 10x7mm, normal (0,-1,0), area 70mm2, adj f33,f44,f52,f59
  f46: cylinder r=19.8mm len=21.94mm, axis (0,0,1), area 162.8mm2, adj f33,f47,f52,f58
  f47: plane 7x2.27mm, normal (0.71,0.71,0), area 22.5mm2, adj f33,f46,f48,f52
  f48: cylinder r=3.9mm len=7mm, axis (0,0,1), area 85.8mm2, adj f33,f47,f49,f52
  f49: plane 7x2.27mm, normal (-0.71,-0.71,0), area 22.5mm2, adj f33,f48,f50,f52
  f50: cylinder r=19.8mm len=22.35mm, axis (0,0,1), area 166.2mm2, adj f33,f49,f51,f52,f102
  f51: plane 7x2.04mm, normal (-0.57,0.82,0), area 17.4mm2, adj f33,f41,f50,f52
  f52: plane 40x40mm, normal (0,0,1), area 158.1mm2, adj f23,f31,f32,f34,f35,f36,f37,f38
  f53: cylinder r=3.9mm len=7.09mm, axis (0,0,1), area 85.8mm2, adj f33,f52,f54,f61
  f54: plane 7x2.04mm, normal (0.57,0.82,0), area 17.4mm2, adj f33,f52,f53,f55
  f55: cylinder r=19.8mm len=22.35mm, axis (0,0,1), area 166.2mm2, adj f33,f52,f54,f56
  f56: plane 7x2.27mm, normal (0.71,-0.71,0), area 22.5mm2, adj f33,f52,f55,f57
  f57: cylinder r=3.9mm len=7mm, axis (0,0,1), area 85.8mm2, adj f33,f52,f56,f58
  f58: plane 7x2.27mm, normal (-0.71,0.71,0), area 22.5mm2, adj f33,f46,f52,f57
  f59: plane 7x4.69mm, normal (0.49,-0.87,0), area 37.7mm2, adj f33,f45,f52,f60
  f60: cylinder r=19.8mm len=7mm, axis (0,0,1), area 5.8mm2, adj f33,f52,f59,f61
  f61: plane 7x3.35mm, normal (-0.57,-0.82,0), area 28.6mm2, adj f33,f52,f53,f60
  f62: cylinder r=1.4mm len=10mm, axis (0,0,1), area 88mm2, adj f33,f40
  f63: cylinder r=1.4mm len=10mm, axis (0,0,1), area 88mm2, adj f33,f40
  f64: cylinder r=1.4mm len=10mm, axis (0,0,1), area 88mm2, adj f33,f40
  f65: cylinder r=1.4mm len=10mm, axis (0,0,1), area 88mm2, adj f33,f40
  f66: plane 8.13x1mm, normal (-1,0,0), area 8.1mm2, adj f27,f28,f40,f68,f76
  f67: plane 8.13x1mm, normal (1,0,0), area 8.1mm2, adj f27,f28,f30,f40,f73
  f68: cylinder r=11mm len=15.31mm, axis (0,0,-1), area 20.5mm2, adj f40,f66,f72,f76
  f69: plane 7.04x4.07mm, normal (0.5,0.87,0), area 8.1mm2, adj f26,f28,f30,f40,f73
  f70: plane 7.04x4.07mm, normal (-0.5,-0.87,0), area 8.1mm2, adj f26,f28,f29,f40,f74
  f71: plane 7.04x4.07mm, normal (0.5,-0.87,0), area 8.1mm2, adj f25,f28,f29,f40,f74
  f72: plane 9.91x5.72mm, normal (-0.5,0.87,0), area 18.1mm2, adj f23,f25,f28,f40,f52,f68,f76,f102
  f73: plane 16.82x10.75mm, normal (0,0,-1), area 21.6mm2, adj f24,f30,f67,f69
  f74: plane 19.42x5.45mm, normal (0,0,-1), area 21.6mm2, adj f5,f11,f17,f24,f29,f70,f71
  f75: plane 24x24mm, normal (0,0,1), area 452.4mm2, adj f5,f11,f17,f24
  f76: plane 16.82x10.75mm, normal (0,0,-1), area 21.6mm2, adj f17,f24,f66,f68,f72
  f77: plane 6.5x1mm, normal (0,1,0), area 6.5mm2, adj f24,f78,f79,f80
  f78: bspline ~9.25x9mm, area 9.3mm2, adj f77,f79,f80,f101
  f79: bspline ~9.25x8.11mm, area 66mm2, adj f24,f77,f78,f101
  f80: bspline ~9.25x8.11mm, area 73.6mm2, adj f24,f77,f78,f101
  f81: plane 4.98x4.18mm, normal (-0.64,0.77,0), area 6.5mm2, adj f24,f82,f83,f84
  f82: bspline ~9x8.68mm, area 9.3mm2, adj f81,f83,f84,f97
  f83: bspline ~9.81x9.03mm, area 66mm2, adj f24,f81,f82,f97
  f84: bspline ~9.81x9.03mm, area 73.6mm2, adj f24,f81,f82,f97
  f85: plane 6.4x1.13mm, normal (-0.98,0.17,0), area 6.5mm2, adj f24,f86,f87,f88
  f86: bspline ~9x8.68mm, area 9.3mm2, adj f85,f87,f88,f98
  f87: bspline ~9.81x9.03mm, area 66mm2, adj f24,f85,f86,f98
  f88: bspline ~9.81x9.03mm, area 73.6mm2, adj f24,f85,f86,f98
  f89: plane 5.63x3.25mm, normal (-0.87,-0.5,0), area 6.5mm2, adj f24,f90,f91,f92
  f90: bspline ~9.25x9mm, area 9.3mm2, adj f89,f91,f92,f99
  f91: bspline ~8.72x8.09mm, area 66mm2, adj f24,f89,f90,f99
  f92: bspline ~9.25x8.11mm, area 73.6mm2, adj f24,f89,f90,f99
  f93: plane 6.11x2.22mm, normal (-0.34,-0.94,0), area 6.5mm2, adj f24,f94,f95,f96
  f94: bspline ~9x7.84mm, area 9.3mm2, adj f93,f95,f96,f100
  f95: bspline ~10.07x9.67mm, area 66mm2, adj f24,f93,f94,f100
  f96: bspline ~10.07x9.67mm, area 73.6mm2, adj f24,f93,f94,f100
  f97: bspline ~8.36x2.24mm, area 6.5mm2, adj f24,f82,f83,f84
  f98: bspline ~6.89x5.95mm, area 6.5mm2, adj f24,f86,f87,f88
  f99: bspline ~8.36x1.01mm, area 6.5mm2, adj f24,f90,f91,f92
  f100: bspline ~6.89x5.96mm, area 6.5mm2, adj f24,f94,f95,f96
  f101: bspline ~7.6x4.83mm, area 6.5mm2, adj f24,f78,f79,f80
  f102: plane 1.26x1.03mm, normal (0,0,-1), area 0.7mm2, adj f28,f50,f72,f103
  f103: plane 3x2.45mm, normal (0.5,-0.87,0), area 8.5mm2, adj f28,f37,f40,f52,f102
PART D: same geometry as B
PLACE A at identity fixed
PLACE B rot(axis=(0.61,0.61,0.5),126.4deg) t=(1.17,-21,50.14)mm
PLACE C rot(axis=(-0.58,-0.58,0.58),120deg) t=(-5,-21,20.81)mm
PLACE D rot(axis=(-0.58,-0.58,0.58),120deg) t=(226,-21,-6.25)mm
MATE fastened C.f39 <-> A.f39  axis (1,0,0) through (-5,-37,36.81)mm
